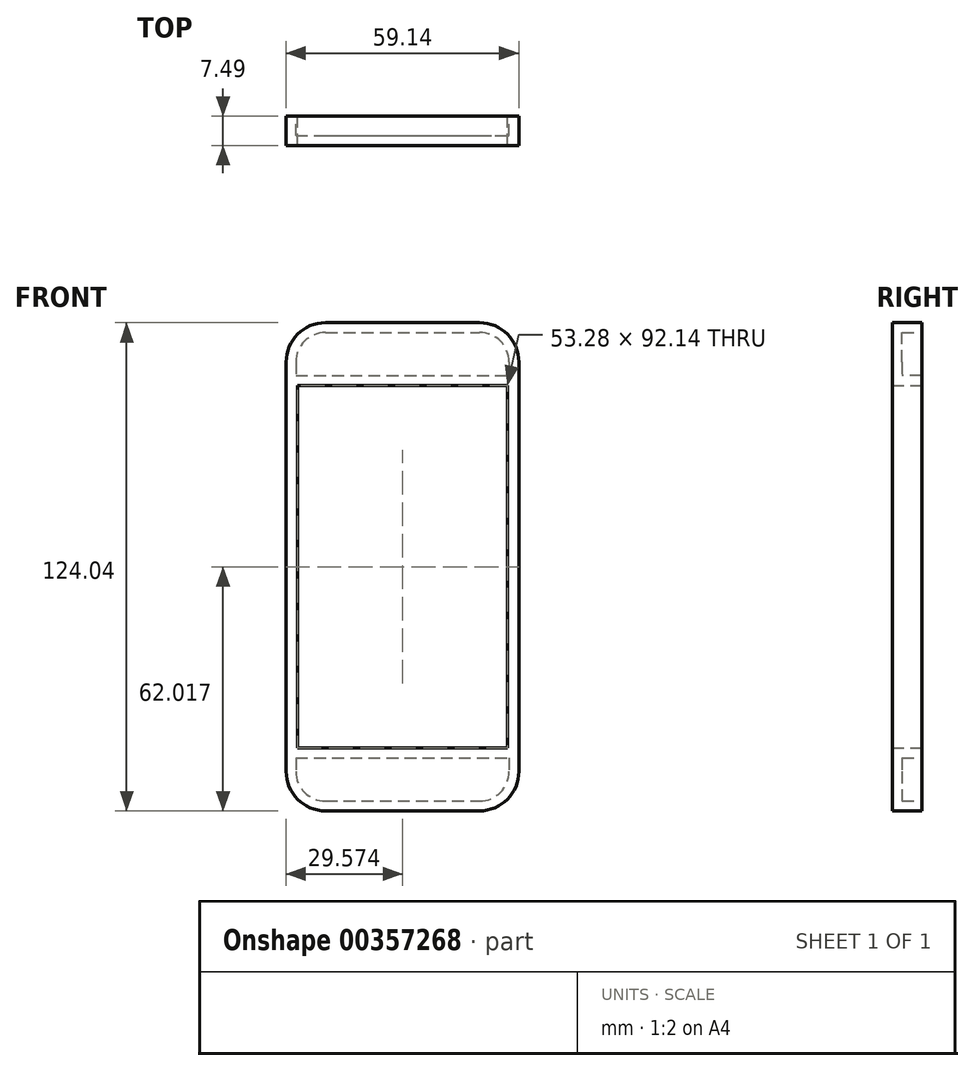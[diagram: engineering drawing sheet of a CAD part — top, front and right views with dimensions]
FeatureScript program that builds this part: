
annotation { "Feature Type Name" : "Feature", "Feature Type Description" : "" }
export const myFeature = defineFeature(function(context is Context, id is Id, definition is map)
    precondition{}
    {
        {
            var Q0;
            Q0=qCreatedBy(makeId("Front.planeOp"),FACE);
            var sketch = newSketch(context, id + "F0", { "sketchPlane" : qUnion([Q0])});
            skLineSegment(sketch, "E0.bottom", {"start": v(-29.43, 62.15) * mm, "end": v(9.71, 62.15) * mm});
            skLineSegment(sketch, "E0.top", {"start": v(-29.43, -61.9) * mm, "end": v(9.71, -61.9) * mm});
            skLineSegment(sketch, "E0.left", {"start": v(-39.43, 52.15) * mm, "end": v(-39.43, -51.9) * mm});
            skLineSegment(sketch, "E0.right", {"start": v(19.71, 52.15) * mm, "end": v(19.71, -51.9) * mm});
            skLineSegment(sketch, "E1.bottom", {"start": v(-36.5, 46.2) * mm, "end": v(16.78, 46.2) * mm});
            skLineSegment(sketch, "E1.top", {"start": v(-36.5, -45.94) * mm, "end": v(16.78, -45.94) * mm});
            skLineSegment(sketch, "E1.left", {"start": v(-36.5, 46.2) * mm, "end": v(-36.5, -45.94) * mm});
            skLineSegment(sketch, "E1.right", {"start": v(16.78, 46.2) * mm, "end": v(16.78, -45.94) * mm});
            skPoint(sketch, "E2.visualSharp", {"position": v(-39.43, 62.15) * mm});
            skArc(sketch, "E2.filletArc", {"start": v(-29.43, 62.15) * mm, "mid": v(-36.5, 59.22) * mm, "end": v(-39.43, 52.15) * mm});
            skPoint(sketch, "E3.visualSharp", {"position": v(19.71, 62.15) * mm});
            skArc(sketch, "E3.filletArc", {"start": v(19.71, 52.15) * mm, "mid": v(16.78, 59.22) * mm, "end": v(9.71, 62.15) * mm});
            skPoint(sketch, "E4.visualSharp", {"position": v(-39.43, -61.9) * mm});
            skArc(sketch, "E4.filletArc", {"start": v(-39.43, -51.9) * mm, "mid": v(-36.5, -58.96) * mm, "end": v(-29.43, -61.9) * mm});
            skPoint(sketch, "E5.visualSharp", {"position": v(19.71, -61.9) * mm});
            skArc(sketch, "E5.filletArc", {"start": v(9.71, -61.9) * mm, "mid": v(16.78, -58.96) * mm, "end": v(19.71, -51.9) * mm});
            skPoint(sketch, "E6.centerSnap0", {"position": v(-9.86, -61.9) * mm});
            skPoint(sketch, "E7.centerSnap0", {"position": v(-9.86, 46.2) * mm});
            skSolve(sketch);
        }
        {
            var Q0;
            Q0=makeQuery(id+"F0.imprint","IMPRINT",FACE,{"disambiguationData":[TD([[makeQuery(id+"F0.imprint","IMPRINT",EDGE,{"derivedFrom":sQuery(id+"F0.wireOp",EDGE,"E0.bottom")}),-1.0]])]});
            extrude(context, id + "F1", {"entities" : qUnion([Q0]), "depth" : 7.5 * mm});
        }
        {
            var Q0;
            Q0=makeQuery(id+"FgzkjZdVnlr3vIU_1.opExtrude","SWEPT_FACE",FACE,{"disambiguationData":[OSD([sQuery(id+"F0.wireOp",EDGE,"E0.right")])]});
            var Q1;
            {var subQ0=sQuery(id+"F0.wireOp",EDGE,"E6");var subQ1=sQuery(id+"F0.wireOp",EDGE,"E1.right");var subQ2=sQuery(id+"F0.wireOp",EDGE,"E1.left");var subQ3=sQuery(id+"F0.wireOp",EDGE,"E1.top");var subQ4=sQuery(id+"F0.wireOp",EDGE,"E1.bottom");Q1=makeQuery(id+"FUl8M8qJuQlzQMs_1.boolean.opBoolean","MERGE",FACE,{"derivedFrom":[makeQuery(id+"FgzkjZdVnlr3vIU_1.boolean.opBoolean","MERGE",FACE,{"derivedFrom":[makeQuery(id+"F1.opExtrude","CAP_FACE",FACE,{"disambiguationData":[OSD([subQ4,subQ3,subQ2,subQ1])],"isStart":true}),makeQuery(id+"FgzkjZdVnlr3vIU_1.opExtrude","CAP_FACE",FACE,{"disambiguationData":[OSD([sQuery(id+"F0.wireOp",EDGE,"E0.bottom"),sQuery(id+"F0.wireOp",EDGE,"E0.top"),sQuery(id+"F0.wireOp",EDGE,"E0.left"),sQuery(id+"F0.wireOp",EDGE,"E0.right"),subQ4,subQ3,subQ2,subQ1,sQuery(id+"F0.wireOp",EDGE,"E2.filletArc"),sQuery(id+"F0.wireOp",EDGE,"E3.filletArc"),sQuery(id+"F0.wireOp",EDGE,"E4.filletArc"),sQuery(id+"F0.wireOp",EDGE,"E5.filletArc"),subQ0,sQuery(id+"F0.wireOp",EDGE,"E7")])],"isStart":true})]}),makeQuery(id+"FUl8M8qJuQlzQMs_1.opExtrude","CAP_FACE",FACE,{"disambiguationData":[OSD([subQ0])],"isStart":true})]});}
            var Q2;
            Q2=makeQuery(id+"FgzkjZdVnlr3vIU_1.opExtrude","SWEPT_FACE",FACE,{"disambiguationData":[OSD([sQuery(id+"F0.wireOp",EDGE,"E0.left")])]});
            shell(context, id + "F2", {"entities" : qUnion([Q0, Q1, Q2]), "thickness" : 2.5 * mm});
        }
    });
